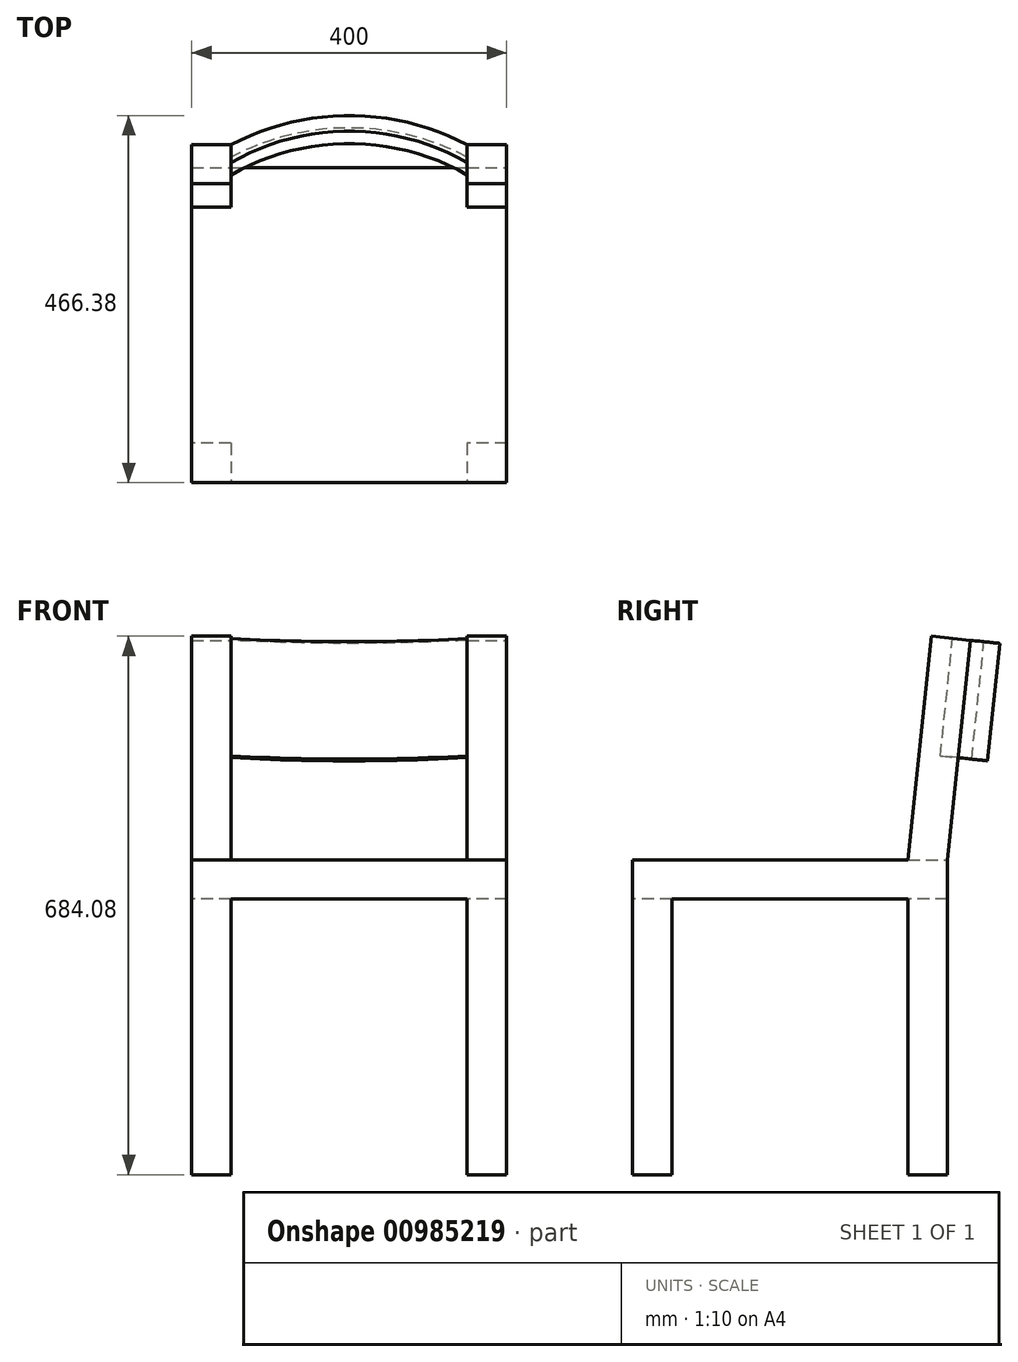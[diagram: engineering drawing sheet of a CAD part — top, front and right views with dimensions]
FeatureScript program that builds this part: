
annotation { "Feature Type Name" : "Feature", "Feature Type Description" : "" }
export const myFeature = defineFeature(function(context is Context, id is Id, definition is map)
    precondition{}
    {
        {
            var Q0;
            Q0=qCreatedBy(makeId("Top.planeOp"),FACE);
            var sketch = newSketch(context, id + "F0", { "sketchPlane" : qUnion([Q0])});
            skLineSegment(sketch, "E0.bottom", {"start": v(-200, 200) * mm, "end": v(200, 200) * mm});
            skLineSegment(sketch, "E0.top", {"start": v(-200, -200) * mm, "end": v(200, -200) * mm});
            skLineSegment(sketch, "E0.left", {"start": v(-200, 200) * mm, "end": v(-200, -200) * mm});
            skLineSegment(sketch, "E0.right", {"start": v(200, 200) * mm, "end": v(200, -200) * mm});
            skPoint(sketch, "E0.middle", {"position": v(0, 0) * mm});
            skSolve(sketch);
        }
        {
            var Q0;
            Q0=makeQuery(id+"F0.imprint","IMPRINT",FACE,{"disambiguationData":[TD([[makeQuery(id+"F0.imprint","IMPRINT",EDGE,{"derivedFrom":sQuery(id+"F0.wireOp",EDGE,"E0.bottom")}),-1.0]])]});
            extrude(context, id + "F1", {"entities" : qUnion([Q0]), "depth" : 400 * mm, "offsetDistance" : 25 * mm});
        }
        {
            var Q0;
            Q0=makeQuery(id+"F1.opExtrude","SWEPT_FACE",FACE,{"disambiguationData":[OSD([sQuery(id+"F0.wireOp",EDGE,"E0.top")])]});
            var sketch = newSketch(context, id + "F2", { "sketchPlane" : qUnion([Q0])});
            skLineSegment(sketch, "E1.bottom", {"start": v(150, 350) * mm, "end": v(-150, 350) * mm});
            skLineSegment(sketch, "E1.top", {"start": v(150, 0) * mm, "end": v(-150, 0) * mm});
            skLineSegment(sketch, "E1.left", {"start": v(150, 350) * mm, "end": v(150, 0) * mm});
            skLineSegment(sketch, "E1.right", {"start": v(-150, 350) * mm, "end": v(-150, 0) * mm});
            skPoint(sketch, "E1.middle", {"position": v(0, 175) * mm});
            skSolve(sketch);
        }
        {
            var Q0;
            Q0=makeQuery(id+"F2.imprint","IMPRINT",FACE,{"disambiguationData":[TD([[makeQuery(id+"F2.imprint","IMPRINT",EDGE,{"derivedFrom":sQuery(id+"F2.wireOp",EDGE,"E1.bottom")}),1.0]])]});
            extrude(context, id + "F3", {"entities" : qUnion([Q0]), "operationType" : NewBodyOperationType.REMOVE, "endBound" : BoundingType.THROUGH_ALL, "oppositeDirection" : true, "depth" : 25 * mm, "offsetDistance" : 25 * mm});
        }
        {
            var Q0;
            Q0=makeQuery(id+"F1.opExtrude","SWEPT_FACE",FACE,{"disambiguationData":[OSD([sQuery(id+"F0.wireOp",EDGE,"E0.left")])]});
            var sketch = newSketch(context, id + "F4", { "sketchPlane" : qUnion([Q0])});
            skLineSegment(sketch, "E2.bottom", {"start": v(-150, 0) * mm, "end": v(150, 0) * mm});
            skLineSegment(sketch, "E2.top", {"start": v(-150, 350) * mm, "end": v(150, 350) * mm});
            skLineSegment(sketch, "E2.left", {"start": v(-150, 0) * mm, "end": v(-150, 350) * mm});
            skLineSegment(sketch, "E2.right", {"start": v(150, 0) * mm, "end": v(150, 350) * mm});
            skPoint(sketch, "E2.middle", {"position": v(0, 175) * mm});
            skSolve(sketch);
        }
        {
            var Q0;
            Q0=makeQuery(id+"F4.imprint","IMPRINT",FACE,{"disambiguationData":[TD([[makeQuery(id+"F4.imprint","IMPRINT",EDGE,{"derivedFrom":sQuery(id+"F4.wireOp",EDGE,"E2.bottom")}),1.0]])]});
            extrude(context, id + "F5", {"entities" : qUnion([Q0]), "operationType" : NewBodyOperationType.REMOVE, "endBound" : BoundingType.THROUGH_ALL, "oppositeDirection" : true, "depth" : 25 * mm, "offsetDistance" : 25 * mm});
        }
        {
            var Q0;
            Q0=makeQuery(id+"F1.opExtrude","CAP_FACE",FACE,{"disambiguationData":[OSD([sQuery(id+"F0.wireOp",EDGE,"E0.bottom"),sQuery(id+"F0.wireOp",EDGE,"E0.top"),sQuery(id+"F0.wireOp",EDGE,"E0.left"),sQuery(id+"F0.wireOp",EDGE,"E0.right")])],"isStart":false});
            cPlane(context, id + "F6", {"entities" : qUnion([Q0]), "cplaneType" : CPlaneType.OFFSET, "offset" : 0 * mm, "width" : 150 * mm, "height" : 150 * mm});
        }
        {
            var Q0;
            Q0=qCreatedBy(id+"F6.planeOp",FACE);
            var sketch = newSketch(context, id + "F7", { "sketchPlane" : qUnion([Q0])});
            skLineSegment(sketch, "E3", {"start": v(512, 200) * mm, "end": v(-410.7, 200) * mm, "construction": true});
            skSolve(sketch);
        }
        {
            var Q0;
            Q0=sQuery(id+"F7.wireOp",EDGE,"E3");
            cPlane(context, id + "F8", {"entities" : qUnion([Q0]), "cplaneType" : CPlaneType.LINE_ANGLE, "offset" : 0 * mm, "angle" : 6 * degree, "width" : 150 * mm, "height" : 150 * mm});
        }
        {
            var Q0;
            Q0=qCreatedBy(id+"F8.planeOp",FACE);
            var sketch = newSketch(context, id + "F9", { "sketchPlane" : qUnion([Q0])});
            skLineSegment(sketch, "E4.bottom", {"start": v(-200, 699.1) * mm, "end": v(200, 699.1) * mm});
            skLineSegment(sketch, "E4.top", {"start": v(-200, 418.71) * mm, "end": v(200, 418.71) * mm});
            skLineSegment(sketch, "E4.left", {"start": v(-200, 699.1) * mm, "end": v(-200, 418.71) * mm});
            skLineSegment(sketch, "E4.right", {"start": v(200, 699.1) * mm, "end": v(200, 418.71) * mm});
            skSolve(sketch);
        }
        {
            var Q0;
            Q0 = qSketchRegion(id + "F9", true);
            extrude(context, id + "F10", {"entities" : qUnion([Q0]), "depth" : 50 * mm, "offsetDistance" : 25 * mm});
        }
        {
            var Q0;
            Q0=makeQuery(id+"F10.opExtrude","CAP_FACE",FACE,{"disambiguationData":[OSD([sQuery(id+"F9.wireOp",EDGE,"E4.bottom"),sQuery(id+"F9.wireOp",EDGE,"E4.top"),sQuery(id+"F9.wireOp",EDGE,"E4.left"),sQuery(id+"F9.wireOp",EDGE,"E4.right")])],"isStart":false});
            var sketch = newSketch(context, id + "F11", { "sketchPlane" : qUnion([Q0])});
            skLineSegment(sketch, "E5.bottom", {"start": v(-150, 699.1) * mm, "end": v(150, 699.1) * mm});
            skLineSegment(sketch, "E5.top", {"start": v(-150, 418.71) * mm, "end": v(150, 418.71) * mm});
            skLineSegment(sketch, "E5.left", {"start": v(-150, 699.1) * mm, "end": v(-150, 418.71) * mm});
            skLineSegment(sketch, "E5.right", {"start": v(150, 699.1) * mm, "end": v(150, 418.71) * mm});
            skSolve(sketch);
        }
        {
            var Q0;
            Q0 = qSketchRegion(id + "F11", true);
            extrude(context, id + "F12", {"entities" : qUnion([Q0]), "operationType" : NewBodyOperationType.REMOVE, "endBound" : BoundingType.THROUGH_ALL, "oppositeDirection" : true, "depth" : 25 * mm, "offsetDistance" : 25 * mm});
        }
        {
            var Q0;
            {var subQ0=sQuery(id+"F9.wireOp",EDGE,"E4.right");var subQ3=sQuery(id+"F9.wireOp",EDGE,"E4.bottom");Q0=makeQuery(id+"F12.boolean.opBoolean","SPLIT",FACE,{"disambiguationData":[TD([makeQuery(id+"F10.opExtrude","SWEPT_FACE",FACE,{"disambiguationData":[OSD([subQ0])]})])],"derivedFrom":makeQuery(id+"F10.opExtrude","SWEPT_FACE",FACE,{"disambiguationData":[OSD([subQ3])]})});}
            cPlane(context, id + "F13", {"entities" : qUnion([Q0]), "cplaneType" : CPlaneType.OFFSET, "offset" : 0 * mm, "width" : 150 * mm, "height" : 150 * mm});
        }
        {
            var Q0;
            Q0=qCreatedBy(id+"F13.planeOp",FACE);
            var sketch = newSketch(context, id + "F14", { "sketchPlane" : qUnion([Q0])});
            skArc(sketch, "E6", {"start": v(150, 157.1) * mm, "mid": v(0, 194.37) * mm, "end": v(-150, 157.1) * mm});
            skArc(sketch, "E7.0", {"start": v(150, 134.25) * mm, "mid": v(0, 174.37) * mm, "end": v(-150, 134.25) * mm});
            skLineSegment(sketch, "E8", {"start": v(150, 157.1) * mm, "end": v(150, 134.25) * mm});
            skLineSegment(sketch, "E9", {"start": v(-150, 157.1) * mm, "end": v(-150, 134.25) * mm});
            skSolve(sketch);
        }
        {
            var Q0;
            Q0 = qSketchRegion(id + "F14", true);
            extrude(context, id + "F15", {"entities" : qUnion([Q0]), "oppositeDirection" : true, "depth" : 150 * mm, "offsetDistance" : 25 * mm});
        }
        {
            var Q0;
            {var subQ0=sQuery(id+"F9.wireOp",EDGE,"E4.right");var subQ2=sQuery(id+"F9.wireOp",EDGE,"E4.top");Q0=makeQuery(id+"F12.boolean.opBoolean","SPLIT",FACE,{"disambiguationData":[TD([makeQuery(id+"F10.opExtrude","SWEPT_FACE",FACE,{"disambiguationData":[OSD([subQ0])]})])],"derivedFrom":makeQuery(id+"F10.opExtrude","SWEPT_FACE",FACE,{"disambiguationData":[OSD([subQ2])]})});}
            extrude(context, id + "F16", {"entities" : qUnion([Q0]), "operationType" : NewBodyOperationType.ADD, "endBound" : BoundingType.UP_TO_NEXT, "depth" : 5.3 * mm, "offsetDistance" : 25 * mm});
        }
        {
            var Q0;
            {var subQ1=sQuery(id+"F9.wireOp",EDGE,"E4.left");var subQ2=sQuery(id+"F9.wireOp",EDGE,"E4.top");Q0=makeQuery(id+"F12.boolean.opBoolean","SPLIT",FACE,{"disambiguationData":[TD([makeQuery(id+"F10.opExtrude","SWEPT_FACE",FACE,{"disambiguationData":[OSD([subQ1])]})])],"derivedFrom":makeQuery(id+"F10.opExtrude","SWEPT_FACE",FACE,{"disambiguationData":[OSD([subQ2])]})});}
            extrude(context, id + "F17", {"entities" : qUnion([Q0]), "operationType" : NewBodyOperationType.ADD, "endBound" : BoundingType.UP_TO_NEXT, "depth" : 7.4 * mm, "offsetDistance" : 25 * mm});
        }
    });
